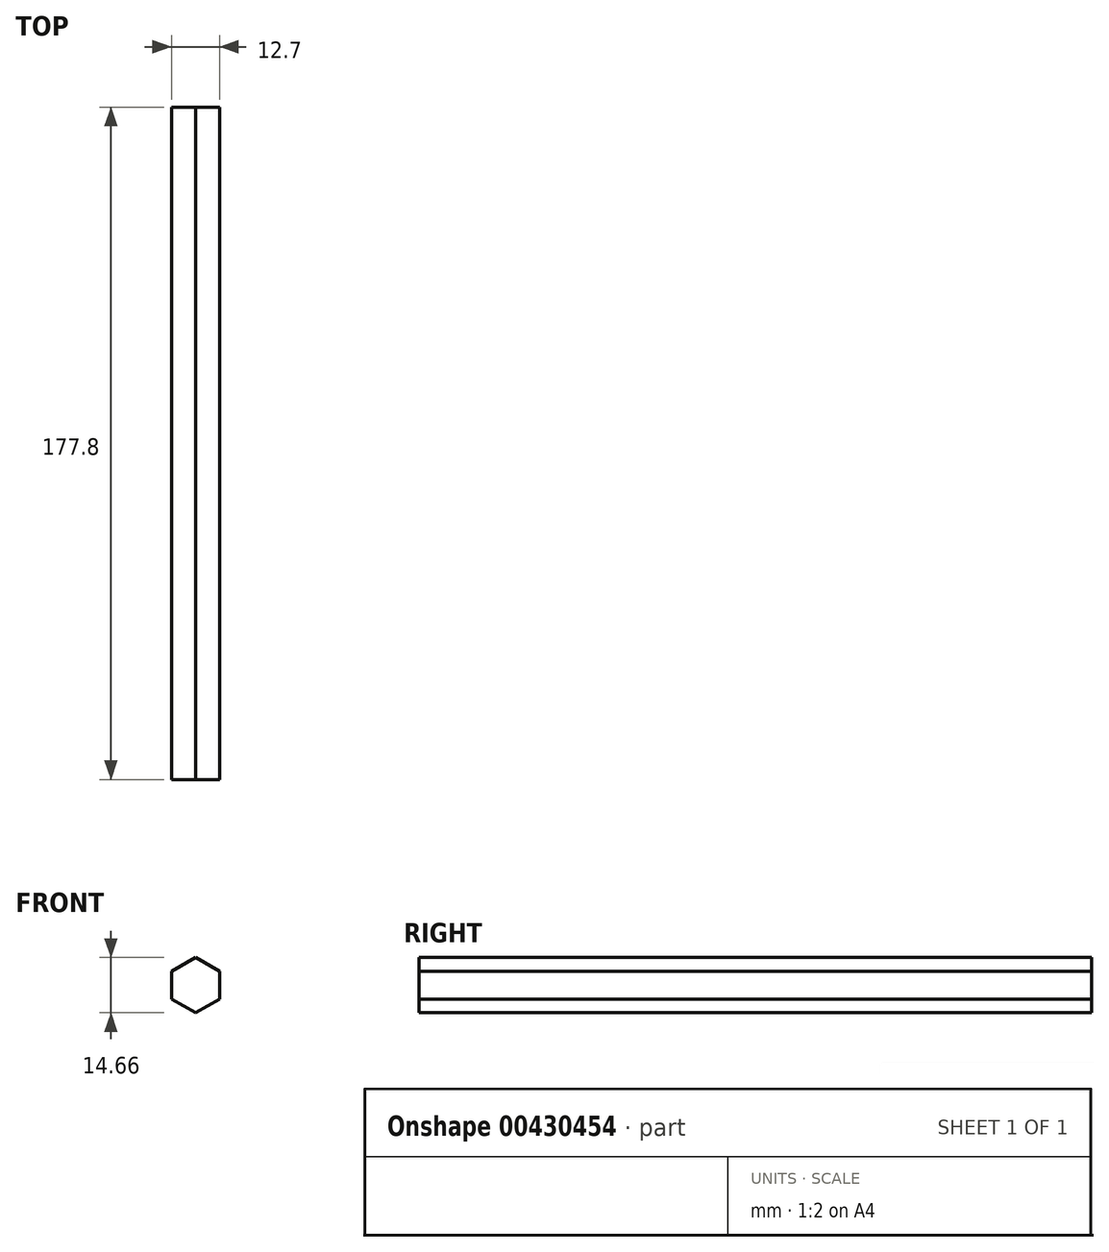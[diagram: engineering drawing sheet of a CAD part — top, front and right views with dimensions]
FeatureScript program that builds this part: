
annotation { "Feature Type Name" : "Feature", "Feature Type Description" : "" }
export const myFeature = defineFeature(function(context is Context, id is Id, definition is map)
    precondition{}
    {
        {
            var Q0;
            Q0=qCreatedBy(makeId("Front.planeOp"),FACE);
            var sketch = newSketch(context, id + "F0", { "sketchPlane" : qUnion([Q0])});
            skCircle(sketch, "E0.cCircle", {"center": v(0, 0) * mm, "radius": 6.35 * mm, "construction": true});
            skLineSegment(sketch, "E0.0", {"start": v(6.35, 3.67) * mm, "end": v(6.35, -3.67) * mm});
            skLineSegment(sketch, "E0.1", {"start": v(6.35, -3.67) * mm, "end": v(0, -7.33) * mm});
            skLineSegment(sketch, "E0.2", {"start": v(0, -7.33) * mm, "end": v(-6.35, -3.67) * mm});
            skLineSegment(sketch, "E0.3", {"start": v(-6.35, -3.67) * mm, "end": v(-6.35, 3.67) * mm});
            skLineSegment(sketch, "E0.4", {"start": v(-6.35, 3.67) * mm, "end": v(0, 7.33) * mm});
            skLineSegment(sketch, "E0.5", {"start": v(0, 7.33) * mm, "end": v(6.35, 3.67) * mm});
            skPoint(sketch, "E0.0.midPoint", {"position": v(6.35, 0) * mm});
            skSolve(sketch);
        }
        {
            var Q0;
            Q0 = qSketchRegion(id + "F0", true);
            extrude(context, id + "F1", {"entities" : qUnion([Q0]), "depth" : 177.8 * mm});
        }
    });
